# Revit family: Window-Exterior-Simpson-Craftsman-Transom
name_source: partatom
category: Windows
revit_build: Autodesk Revit Architecture 2012 (Build: 20110916_2132(x64)
units: mm (PartAtom-declared; Revit-internal decimal feet)

## types (13) — shared parameters
Assembly Code = B2020100
Default Sill Height = 70"
Glass = Glass - Simpson Doors - Clear
Glass Options = http://simpsondoor.com
Glass Thickness = 3/4"
Height = 14"
Manufacturer = Simpson Door Company
Notes = Dozens of glass textures and colors are available. For a list of standard options visit the Simpson web site or submit a custom glass request: http://simpsondoor.com
Panel = Wood - Simpson Doors - Douglas Fir
Panel Stile Width = 5"
Panel Thickness = 1 3/4"
Product Documentation Link = http://www.simpsondoor.com
Product Page URL = http://www.simpsondoor.com
URL = http://www.simpsondoor.com
UltraBlock Note = This Door Comes with The Option of UltraBlock Technology. It is Turn On as a Default
UltraBlock Opion = Yes
Wall Closure = By host
WaterBarrier Note = This Door Comes with The Option of WaterBarrier with UltraBlock Technology. It is Turn Off as a Default
WaterBarrier with UltraBlock Technology = No
Wood Species = http://simpsondoor.com
Wood Species Note = Available in Any Wood Species

## per-type parameters (varying)
| type | Bottom Rail Height | Description | Model | Sub-Series | Top Rail Height | Width |
| 6784 Holbrook Transom 36x14 | 2 13/16" | 3'-0" Holbrook Transom | 6784 | Holbrook | 2 13/16" | 36" |
| 6784 Holbrook Transom 72.75x14 | 2" | 6'-0" Holbrook Transom | 6784 | Holbrook | 2" | 72 3/4" |
| 6786 Four Square Transom 36x14 | 2 13/16" | 3'-0" Four Square Transom | 6786 | Four Square | 2 13/16" | 36" |
| 6786 Four Square Transom 72.75x14 | 2" | 6'-0" Four Square Transom | 6786 | Four Square | 2" | 72 3/4" |
| 6787 Solano Transom 36x14 | 2 13/16" | 3'-0" Solano Transom | 6787 | Solano | 2 13/16" | 36" |
| 6787 Solano Transom 72.75x14 | 2" | 6'-0" Solano Transom | 6787 | Solano | 2" | 72 3/4" |
| 6789 Ravenna Transom 36x14 | 2 13/16" | 3'-0" Ravenna Transom | 6789 | Ravenna | 2 13/16" | 36" |
| 6789 Ravenna Transom 72.75x14 | 2" | 6'-0" Ravenna Transom | 6789 | Ravenna | 2" | 72 3/4" |
| 6781 California Poppy Transom 72.75x14 | 2" | 6'-0" California Poppy Transom | 6781 | California Poppy | 2" | 72 3/4" |
| 6782 Scottsdale Cactus Transom 72.75x14 | 2" | 6'-0" Scottsdale Cactus Transom | 6782 | Scottsdale Cactus | 2" | 72 3/4" |
| 6785 Northwest Garden Transom 72.75x14 | 2" | 6'-0" Northwest Garden Transom | 6785 | Northwest Garden | 2" | 72 3/4" |
| 7751 Craftsman Transom 36x14 | 2 13/16" | 3'-0" Craftsman Transom | 7751 | Craftsman | 2 13/16" | 36" |
| 7751 Craftsman Transom 72.75x14 | 2 13/16" | 6'-0" Craftsman Transom | 7751 | Craftsman | 2 13/16" | 72 3/4" |

## geometry (parser evidence)
native form markers: Blend x20, Sweep x5
no freeform markers — native parametric forms only
